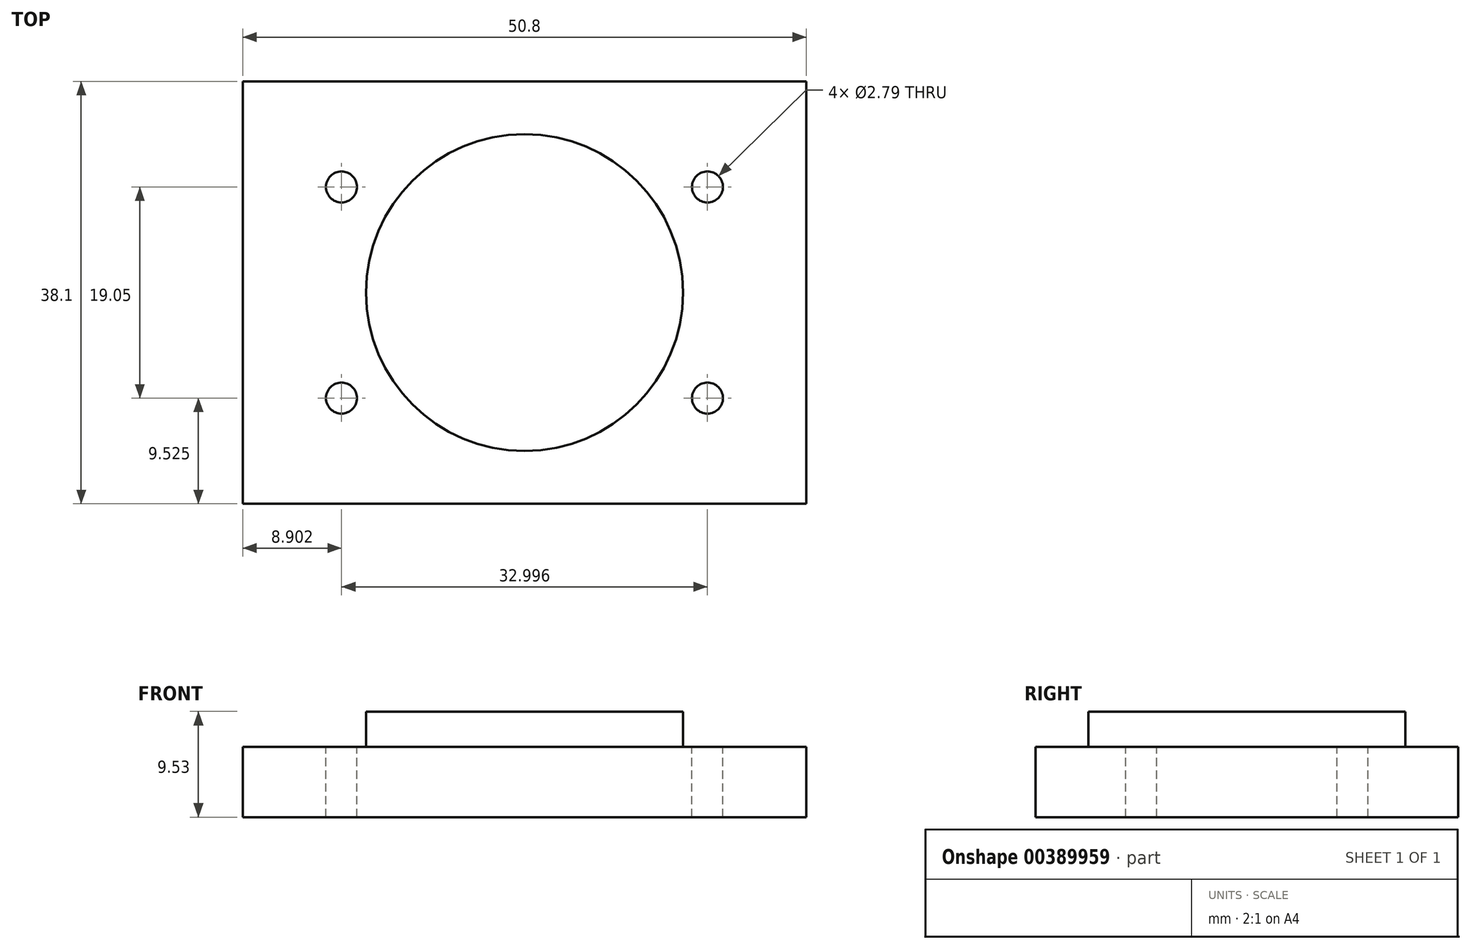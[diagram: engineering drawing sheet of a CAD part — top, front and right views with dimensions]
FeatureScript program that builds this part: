
annotation { "Feature Type Name" : "Feature", "Feature Type Description" : "" }
export const myFeature = defineFeature(function(context is Context, id is Id, definition is map)
    precondition{}
    {
        {
            var Q0;
            Q0=qCreatedBy(makeId("Top.planeOp"),FACE);
            var sketch = newSketch(context, id + "F0", { "sketchPlane" : qUnion([Q0])});
            skLineSegment(sketch, "E0.bottom", {"start": v(0, 0) * mm, "end": v(50.8, 0) * mm});
            skLineSegment(sketch, "E0.top", {"start": v(0, 38.1) * mm, "end": v(50.8, 38.1) * mm});
            skLineSegment(sketch, "E0.left", {"start": v(0, 0) * mm, "end": v(0, 38.1) * mm});
            skLineSegment(sketch, "E0.right", {"start": v(50.8, 0) * mm, "end": v(50.8, 38.1) * mm});
            skSolve(sketch);
        }
        {
            var Q0;
            Q0 = qSketchRegion(id + "F0", true);
            extrude(context, id + "F1", {"entities" : qUnion([Q0]), "depth" : 6.35 * mm});
        }
        {
            var Q0;
            Q0=makeQuery(id+"F1.opExtrude","CAP_FACE",FACE,{"disambiguationData":[OSD([sQuery(id+"F0.wireOp",EDGE,"E0.bottom"),sQuery(id+"F0.wireOp",EDGE,"E0.top"),sQuery(id+"F0.wireOp",EDGE,"E0.left"),sQuery(id+"F0.wireOp",EDGE,"E0.right")])],"isStart":false});
            var sketch = newSketch(context, id + "F2", { "sketchPlane" : qUnion([Q0])});
            skCircle(sketch, "E1", {"center": v(25.4, 19.05) * mm, "radius": 14.29 * mm});
            skPoint(sketch, "E1.centerSnap0", {"position": v(25.4, 0) * mm});
            skPoint(sketch, "E1.centerSnap1", {"position": v(0, 19.05) * mm});
            skSolve(sketch);
        }
        {
            var Q0;
            Q0 = qSketchRegion(id + "F2", true);
            extrude(context, id + "F3", {"entities" : qUnion([Q0]), "operationType" : NewBodyOperationType.ADD, "depth" : 3.17 * mm});
        }
        {
            var Q0;
            Q0=makeQuery(id+"F1.opExtrude","CAP_FACE",FACE,{"disambiguationData":[OSD([sQuery(id+"F0.wireOp",EDGE,"E0.bottom"),sQuery(id+"F0.wireOp",EDGE,"E0.top"),sQuery(id+"F0.wireOp",EDGE,"E0.left"),sQuery(id+"F0.wireOp",EDGE,"E0.right")])],"isStart":false});
            var sketch = newSketch(context, id + "F4", { "sketchPlane" : qUnion([Q0])});
            skLineSegment(sketch, "E2", {"start": v(0, 19.05) * mm, "end": v(25.4, 19.05) * mm, "construction": true});
            skLineSegment(sketch, "E3", {"start": v(25.4, 19.05) * mm, "end": v(8.9, 28.58) * mm, "construction": true});
            skPoint(sketch, "E4.center", {"position": v(25.4, 19.05) * mm});
            skLineSegment(sketch, "E4.anchor1", {"start": v(25.4, 19.05) * mm, "end": v(8.9, 28.57) * mm, "construction": true});
            skCircle(sketch, "E5", {"center": v(8.9, 28.58) * mm, "radius": 1.4 * mm});
            skCircle(sketch, "E6.2.0", {"center": v(41.9, 28.58) * mm, "radius": 1.4 * mm});
            skCircle(sketch, "E6.3.0", {"center": v(41.9, 9.53) * mm, "radius": 1.4 * mm});
            skCircle(sketch, "E6.5.0", {"center": v(8.9, 9.52) * mm, "radius": 1.4 * mm});
            skLineSegment(sketch, "E6.anchor2", {"start": v(25.4, 19.05) * mm, "end": v(8.9, 9.52) * mm, "construction": true});
            skSolve(sketch);
        }
        {
            var Q0;
            Q0 = qSketchRegion(id + "F4", true);
            extrude(context, id + "F5", {"entities" : qUnion([Q0]), "operationType" : NewBodyOperationType.REMOVE, "endBound" : BoundingType.UP_TO_NEXT, "oppositeDirection" : true, "depth" : 25.4 * mm});
        }
    });
